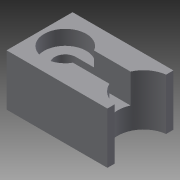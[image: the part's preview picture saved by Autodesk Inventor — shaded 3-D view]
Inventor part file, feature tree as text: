
AUTODESK INVENTOR PART (.ipt)
format: ipt  version: 2015 (Build 190159000, 159)  size: 110,592 bytes
history: native  units: in
note: dims shown in document units (in); Inventor stores cm internally (conversion verified against a paired STEP export)
features: sketch x5, extrude x3, hole x2
ambient origin geometry x8: Origin, YZ Plane, XZ Plane, XY Plane, X Axis, Y Axis, Z Axis, Center Point
bodies: Body1 (feature_tree), Body2 (feature_tree)
feature tree (10):
  extrude  "Extrusion2"  Depth=9.0in
  extrude  "Extrusion3"  Depth=7.0in TaperAngle=0.0deg
  hole  "Hole3"  [1 undecoded]
  hole  "Hole5"  [1 undecoded]
  extrude  "Extrusion5"  [1 undecoded]
  sketch  "Sketch1"  dims[d0=13.75in d1=9.0in]
  sketch  "Sketch2"  dims[d4=7.0in d5=0.0in d10=7.0in d11=0.0in]
  sketch  "Sketch3"  dims[d30=5.75in d31=0.75in d32=0.375in d33=0.25in d34=0.5635in d35=2.0in d36=0.0in]
  sketch  "Sketch4"  dims[d44=2.875in d45=0.75in d46=0.375in d47=0.25in d48=0.5635in d49=2.0in d50=0.0in d54=4.0in d55=0.0in]
  sketch  "Sketch5"
note: 3 required parameter values undecoded (feature->parameter linkage not recoverable at this tier; creation-order binding heuristic only, values carry confidence <= 0.55)
